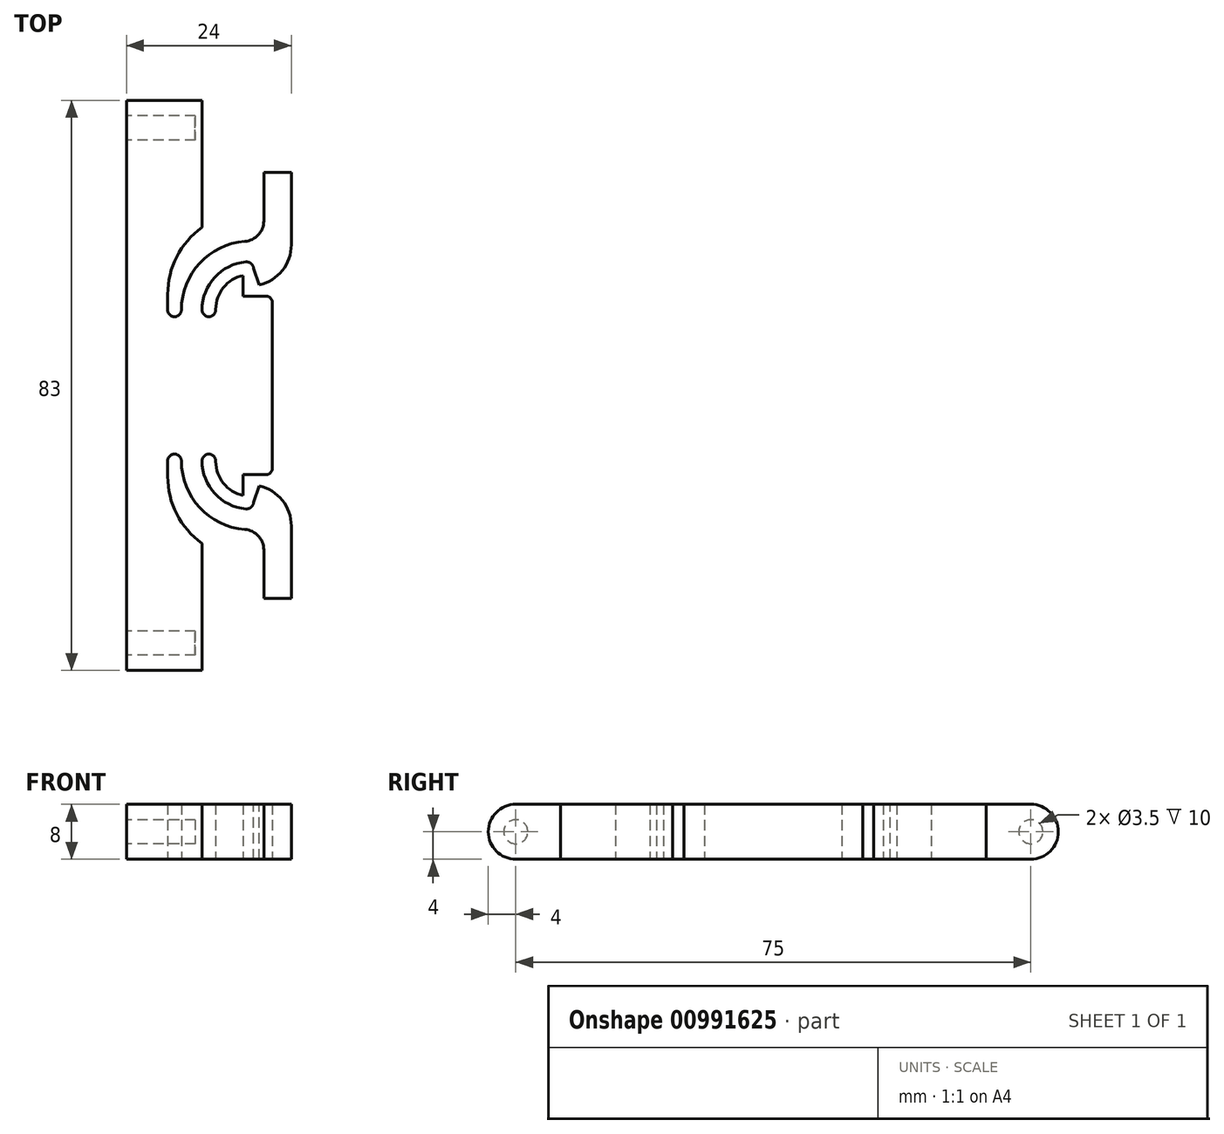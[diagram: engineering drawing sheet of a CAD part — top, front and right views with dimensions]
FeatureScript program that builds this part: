
annotation { "Feature Type Name" : "Feature", "Feature Type Description" : "" }
export const myFeature = defineFeature(function(context is Context, id is Id, definition is map)
    precondition{}
    {
        {
            var Q0;
            Q0=qCreatedBy(makeId("Top.planeOp"),FACE);
            var sketch = newSketch(context, id + "F0", { "sketchPlane" : qUnion([Q0])});
            skLineSegment(sketch, "E0.bottom", {"start": v(0, 0) * mm, "end": v(24, 0) * mm});
            skLineSegment(sketch, "E0.top", {"start": v(0, 83) * mm, "end": v(24, 83) * mm});
            skLineSegment(sketch, "E0.left", {"start": v(0, 0) * mm, "end": v(0, 83) * mm});
            skLineSegment(sketch, "E0.right", {"start": v(24, 0) * mm, "end": v(24, 83) * mm});
            skLineSegment(sketch, "E1", {"start": v(0, 41.5) * mm, "end": v(24, 41.5) * mm, "construction": true});
            skLineSegment(sketch, "E2.bottom", {"start": v(24, 59.5) * mm, "end": v(17, 59.5) * mm});
            skLineSegment(sketch, "E2.top", {"start": v(24, 23.5) * mm, "end": v(17, 23.5) * mm});
            skLineSegment(sketch, "E2.left", {"start": v(24, 59.5) * mm, "end": v(24, 23.5) * mm});
            skLineSegment(sketch, "E2.right", {"start": v(17, 59.5) * mm, "end": v(17, 23.5) * mm});
            skLineSegment(sketch, "E3", {"start": v(18.5, 59.5) * mm, "end": v(18.5, 23.5) * mm, "construction": true});
            skLineSegment(sketch, "E4.bottom", {"start": v(18.5, 59.5) * mm, "end": v(24, 59.5) * mm});
            skLineSegment(sketch, "E4.top", {"start": v(18.5, 56) * mm, "end": v(24, 56) * mm});
            skLineSegment(sketch, "E4.left", {"start": v(18.5, 59.5) * mm, "end": v(18.5, 56) * mm});
            skLineSegment(sketch, "E4.right", {"start": v(24, 59.5) * mm, "end": v(24, 56) * mm});
            skLineSegment(sketch, "E5.bottom", {"start": v(18.5, 23.5) * mm, "end": v(24, 23.5) * mm});
            skLineSegment(sketch, "E5.top", {"start": v(18.5, 27) * mm, "end": v(24, 27) * mm});
            skLineSegment(sketch, "E5.left", {"start": v(18.5, 23.5) * mm, "end": v(18.5, 27) * mm});
            skLineSegment(sketch, "E5.right", {"start": v(24, 23.5) * mm, "end": v(24, 27) * mm});
            skLineSegment(sketch, "E6", {"start": v(11, 83) * mm, "end": v(11, 0) * mm, "construction": true});
            skLineSegment(sketch, "E7.bottom", {"start": v(11, 64.5) * mm, "end": v(24, 64.5) * mm});
            skLineSegment(sketch, "E7.top", {"start": v(11, 62.5) * mm, "end": v(24, 62.5) * mm});
            skLineSegment(sketch, "E7.left", {"start": v(11, 64.5) * mm, "end": v(11, 62.5) * mm});
            skLineSegment(sketch, "E7.right", {"start": v(24, 64.5) * mm, "end": v(24, 62.5) * mm});
            skLineSegment(sketch, "E8.bottom", {"start": v(11, 20.5) * mm, "end": v(24, 20.5) * mm});
            skLineSegment(sketch, "E8.top", {"start": v(11, 18.5) * mm, "end": v(24, 18.5) * mm});
            skLineSegment(sketch, "E8.left", {"start": v(11, 20.5) * mm, "end": v(11, 18.5) * mm});
            skLineSegment(sketch, "E8.right", {"start": v(24, 20.5) * mm, "end": v(24, 18.5) * mm});
            skLineSegment(sketch, "E9.bottom", {"start": v(20, 62.5) * mm, "end": v(24, 62.5) * mm});
            skLineSegment(sketch, "E9.top", {"start": v(20, 72.5) * mm, "end": v(24, 72.5) * mm});
            skLineSegment(sketch, "E9.left", {"start": v(20, 62.5) * mm, "end": v(20, 72.5) * mm});
            skLineSegment(sketch, "E9.right", {"start": v(24, 62.5) * mm, "end": v(24, 72.5) * mm});
            skLineSegment(sketch, "E10.bottom", {"start": v(20, 20.5) * mm, "end": v(24, 20.5) * mm});
            skLineSegment(sketch, "E10.top", {"start": v(20, 10.5) * mm, "end": v(24, 10.5) * mm});
            skLineSegment(sketch, "E10.left", {"start": v(20, 20.5) * mm, "end": v(20, 10.5) * mm});
            skLineSegment(sketch, "E10.right", {"start": v(24, 20.5) * mm, "end": v(24, 10.5) * mm});
            skLineSegment(sketch, "E11.top", {"start": v(11, 73) * mm, "end": v(24, 73) * mm});
            skLineSegment(sketch, "E11.left", {"start": v(11, 64.5) * mm, "end": v(11, 73) * mm});
            skLineSegment(sketch, "E11.right", {"start": v(24, 64.5) * mm, "end": v(24, 73) * mm});
            skLineSegment(sketch, "E12.top", {"start": v(11, 10) * mm, "end": v(24, 10) * mm});
            skLineSegment(sketch, "E12.left", {"start": v(11, 18.5) * mm, "end": v(11, 10) * mm});
            skLineSegment(sketch, "E12.right", {"start": v(24, 18.5) * mm, "end": v(24, 10) * mm});
            skLineSegment(sketch, "E13.bottom", {"start": v(17, 59.5) * mm, "end": v(11, 59.5) * mm});
            skLineSegment(sketch, "E13.top", {"start": v(17, 57.5) * mm, "end": v(11, 57.5) * mm});
            skLineSegment(sketch, "E13.left", {"start": v(17, 59.5) * mm, "end": v(17, 57.5) * mm});
            skLineSegment(sketch, "E13.right", {"start": v(11, 59.5) * mm, "end": v(11, 57.5) * mm});
            skLineSegment(sketch, "E14.bottom", {"start": v(17, 23.5) * mm, "end": v(11, 23.5) * mm});
            skLineSegment(sketch, "E14.top", {"start": v(17, 25.5) * mm, "end": v(11, 25.5) * mm});
            skLineSegment(sketch, "E14.left", {"start": v(17, 23.5) * mm, "end": v(17, 25.5) * mm});
            skLineSegment(sketch, "E14.right", {"start": v(11, 23.5) * mm, "end": v(11, 25.5) * mm});
            skLineSegment(sketch, "E15.bottom", {"start": v(11, 57.5) * mm, "end": v(13, 57.5) * mm});
            skLineSegment(sketch, "E15.top", {"start": v(11, 51.5) * mm, "end": v(13, 51.5) * mm});
            skLineSegment(sketch, "E15.left", {"start": v(11, 57.5) * mm, "end": v(11, 51.5) * mm});
            skLineSegment(sketch, "E15.right", {"start": v(13, 57.5) * mm, "end": v(13, 51.5) * mm});
            skLineSegment(sketch, "E16.bottom", {"start": v(11, 25.5) * mm, "end": v(13, 25.5) * mm});
            skLineSegment(sketch, "E16.top", {"start": v(11, 31.5) * mm, "end": v(13, 31.5) * mm});
            skLineSegment(sketch, "E16.left", {"start": v(11, 25.5) * mm, "end": v(11, 31.5) * mm});
            skLineSegment(sketch, "E16.right", {"start": v(13, 25.5) * mm, "end": v(13, 31.5) * mm});
            skLineSegment(sketch, "E17.bottom", {"start": v(8, 20.5) * mm, "end": v(11, 20.5) * mm});
            skLineSegment(sketch, "E17.top", {"start": v(8, 31.5) * mm, "end": v(11, 31.5) * mm});
            skLineSegment(sketch, "E17.left", {"start": v(8, 20.5) * mm, "end": v(8, 31.5) * mm});
            skLineSegment(sketch, "E17.right", {"start": v(11, 20.5) * mm, "end": v(11, 31.5) * mm});
            skPoint(sketch, "E18.oppositeSnap0", {"position": v(8, 26) * mm});
            skLineSegment(sketch, "E18.bottom", {"start": v(11, 51.5) * mm, "end": v(8, 51.5) * mm});
            skLineSegment(sketch, "E18.top", {"start": v(11, 62.5) * mm, "end": v(8, 62.5) * mm});
            skLineSegment(sketch, "E18.left", {"start": v(11, 51.5) * mm, "end": v(11, 62.5) * mm});
            skLineSegment(sketch, "E18.right", {"start": v(8, 51.5) * mm, "end": v(8, 62.5) * mm});
            skLineSegment(sketch, "E19.bottom", {"start": v(11, 18.5) * mm, "end": v(6, 18.5) * mm});
            skLineSegment(sketch, "E19.top", {"start": v(11, 31.5) * mm, "end": v(6, 31.5) * mm});
            skLineSegment(sketch, "E19.left", {"start": v(11, 18.5) * mm, "end": v(11, 31.5) * mm});
            skLineSegment(sketch, "E19.right", {"start": v(6, 18.5) * mm, "end": v(6, 31.5) * mm});
            skLineSegment(sketch, "E20.bottom", {"start": v(11, 64.5) * mm, "end": v(6, 64.5) * mm});
            skLineSegment(sketch, "E20.top", {"start": v(11, 51.5) * mm, "end": v(6, 51.5) * mm});
            skLineSegment(sketch, "E20.left", {"start": v(11, 64.5) * mm, "end": v(11, 51.5) * mm});
            skLineSegment(sketch, "E20.right", {"start": v(6, 64.5) * mm, "end": v(6, 51.5) * mm});
            skLineSegment(sketch, "E21.top", {"start": v(11, 0) * mm, "end": v(24, 0) * mm});
            skLineSegment(sketch, "E21.left", {"start": v(11, 10) * mm, "end": v(11, 0) * mm});
            skLineSegment(sketch, "E21.right", {"start": v(24, 10) * mm, "end": v(24, 0) * mm});
            skLineSegment(sketch, "E22.top", {"start": v(11, 83) * mm, "end": v(24, 83) * mm});
            skLineSegment(sketch, "E22.left", {"start": v(11, 73) * mm, "end": v(11, 83) * mm});
            skLineSegment(sketch, "E22.right", {"start": v(24, 73) * mm, "end": v(24, 83) * mm});
            skPoint(sketch, "E23.oppositeSnap0", {"position": v(21.25, 27) * mm});
            skLineSegment(sketch, "E23.bottom", {"start": v(17, 54.5) * mm, "end": v(21.25, 54.5) * mm});
            skLineSegment(sketch, "E23.top", {"start": v(17, 28.5) * mm, "end": v(21.25, 28.5) * mm});
            skLineSegment(sketch, "E23.left", {"start": v(17, 54.5) * mm, "end": v(17, 28.5) * mm});
            skLineSegment(sketch, "E23.right", {"start": v(21.25, 54.5) * mm, "end": v(21.25, 28.5) * mm});
            skSolve(sketch);
        }
        {
            var Q0;
            {var subQ7=sQuery(id+"F0.wireOp",EDGE,"E0.left");Q0=makeQuery(id+"F0.imprint","IMPRINT",FACE,{"disambiguationData":[TD([[makeQuery(id+"F0.imprint","IMPRINT",EDGE,{"derivedFrom":subQ7}),-1.0]])]});}
            var Q1;
            {var subQ3=sQuery(id+"F0.wireOp",EDGE,"E9.top");Q1=makeQuery(id+"F0.imprint","IMPRINT",FACE,{"disambiguationData":[TD([[makeQuery(id+"F0.imprint","IMPRINT",EDGE,{"derivedFrom":subQ3}),-1.0]])]});}
            var Q2;
            {var subQ0=sQuery(id+"F0.wireOp",EDGE,"E7.bottom");var subQ1=sQuery(id+"F0.wireOp",EDGE,"E0.right");var subQ2=makeQuery(id+"F0.imprint","INTERSECT",VERTEX,{"derivedFrom":[subQ1,subQ0]});Q2=makeQuery(id+"F0.imprint","IMPRINT",FACE,{"disambiguationData":[TD([[makeQuery(id+"F0.imprint","IMPRINT",EDGE,{"disambiguationData":[TD([[subQ2,1.0]])],"derivedFrom":subQ1}),1.0]])]});}
            var Q3;
            {var subQ3=sQuery(id+"F0.wireOp",EDGE,"E4.top");Q3=makeQuery(id+"F0.imprint","IMPRINT",FACE,{"disambiguationData":[TD([[makeQuery(id+"F0.imprint","IMPRINT",EDGE,{"derivedFrom":subQ3}),1.0]])]});}
            var Q4;
            {var subQ0=sQuery(id+"F0.wireOp",EDGE,"E5.top");Q4=makeQuery(id+"F0.imprint","IMPRINT",FACE,{"disambiguationData":[TD([[makeQuery(id+"F0.imprint","IMPRINT",EDGE,{"derivedFrom":subQ0}),-1.0]])]});}
            var Q5;
            {var subQ0=sQuery(id+"F0.wireOp",EDGE,"E8.bottom");var subQ1=sQuery(id+"F0.wireOp",EDGE,"E0.right");var subQ2=makeQuery(id+"F0.imprint","INTERSECT",VERTEX,{"derivedFrom":[subQ1,subQ0]});Q5=makeQuery(id+"F0.imprint","IMPRINT",FACE,{"disambiguationData":[TD([[makeQuery(id+"F0.imprint","IMPRINT",EDGE,{"disambiguationData":[TD([[subQ2,1.0]])],"derivedFrom":subQ1}),1.0]])]});}
            var Q6;
            {var subQ0=sQuery(id+"F0.wireOp",EDGE,"E10.top");Q6=makeQuery(id+"F0.imprint","IMPRINT",FACE,{"disambiguationData":[TD([[makeQuery(id+"F0.imprint","IMPRINT",EDGE,{"derivedFrom":subQ0}),1.0]])]});}
            var Q7;
            {var subQ3=sQuery(id+"F0.wireOp",EDGE,"E14.bottom");Q7=makeQuery(id+"F0.imprint","IMPRINT",FACE,{"disambiguationData":[TD([[makeQuery(id+"F0.imprint","IMPRINT",EDGE,{"derivedFrom":subQ3}),1.0]])]});}
            var Q8;
            Q8=makeQuery(id+"F0.imprint","IMPRINT",FACE,{"disambiguationData":[TD([[makeQuery(id+"F0.imprint","IMPRINT",EDGE,{"derivedFrom":sQuery(id+"F0.wireOp",EDGE,"E14.right")}),1.0]])]});
            var Q9;
            Q9=makeQuery(id+"F0.imprint","IMPRINT",FACE,{"disambiguationData":[TD([[makeQuery(id+"F0.imprint","IMPRINT",EDGE,{"derivedFrom":sQuery(id+"F0.wireOp",EDGE,"E13.right")}),-1.0]])]});
            var Q10;
            {var subQ0=sQuery(id+"F0.wireOp",EDGE,"E13.bottom");Q10=makeQuery(id+"F0.imprint","IMPRINT",FACE,{"disambiguationData":[TD([[makeQuery(id+"F0.imprint","IMPRINT",EDGE,{"derivedFrom":subQ0}),-1.0]])]});}
            var Q11;
            {var subQ0=sQuery(id+"F0.wireOp",EDGE,"E23.bottom");Q11=makeQuery(id+"F0.imprint","IMPRINT",FACE,{"disambiguationData":[TD([[makeQuery(id+"F0.imprint","IMPRINT",EDGE,{"derivedFrom":subQ0}),-1.0]])]});}
            extrude(context, id + "F1", {"entities" : qUnion([Q0, Q1, Q2, Q3, Q4, Q5, Q6, Q7, Q8, Q9, Q10, Q11]), "depth" : 8 * mm, "offsetDistance" : 25 * mm});
        }
        {
            var Q0;
            Q0=makeQuery(id+"F1.opExtrude","CAP_EDGE",EDGE,{"disambiguationData":[OSD([sQuery(id+"F0.wireOp",EDGE,"E0.top")])],"isStart":false});
            var Q1;
            Q1=makeQuery(id+"F1.opExtrude","CAP_EDGE",EDGE,{"disambiguationData":[OSD([sQuery(id+"F0.wireOp",EDGE,"E0.bottom")])],"isStart":false});
            var Q2;
            Q2=makeQuery(id+"F1.opExtrude","CAP_EDGE",EDGE,{"disambiguationData":[OSD([sQuery(id+"F0.wireOp",EDGE,"E0.bottom")])],"isStart":true});
            var Q3;
            Q3=makeQuery(id+"F1.opExtrude","CAP_EDGE",EDGE,{"disambiguationData":[OSD([sQuery(id+"F0.wireOp",EDGE,"E0.top")])],"isStart":true});
            fillet(context, id + "F2", {"entities" : qUnion([Q0, Q1, Q2, Q3]), "radius" : 4 * mm, "tangentPropagation" : true, "allowEdgeOverflow" : false});
        }
        {
            var Q0;
            Q0=makeQuery(id+"F1.opExtrude","SWEPT_EDGE",EDGE,{"disambiguationData":[OSD([sQuery(id+"F0.wireOp",EDGE,"E0.right"),sQuery(id+"F0.wireOp",EDGE,"E4.top")])]});
            var Q1;
            Q1=makeQuery(id+"F1.opExtrude","SWEPT_EDGE",EDGE,{"disambiguationData":[OSD([sQuery(id+"F0.wireOp",EDGE,"E0.right"),sQuery(id+"F0.wireOp",EDGE,"E5.top")])]});
            fillet(context, id + "F3", {"entities" : qUnion([Q0, Q1]), "radius" : 6 * mm, "tangentPropagation" : true, "allowEdgeOverflow" : false});
        }
        {
            var Q0;
            Q0=makeQuery(id+"F3.opFillet","BLEND_EDGE",EDGE,{"blendedFrom":[makeQuery(id+"F1.opExtrude","SWEPT_EDGE",EDGE,{"disambiguationData":[OSD([sQuery(id+"F0.wireOp",EDGE,"E0.right"),sQuery(id+"F0.wireOp",EDGE,"E4.top")])]}),makeQuery(id+"F1.opExtrude","SWEPT_FACE",FACE,{"disambiguationData":[OSD([sQuery(id+"F0.wireOp",EDGE,"E4.left")])]})],"blendedInto":[makeQuery(id+"F1.opExtrude","SWEPT_FACE",FACE,{"disambiguationData":[OSD([sQuery(id+"F0.wireOp",EDGE,"E4.left")])]})]});
            chamfer(context, id + "F4", {"entities" : qUnion([Q0]), "chamferType" : ChamferType.TWO_OFFSETS, "width1" : 0.5 * mm, "oppositeDirection" : false, "width2" : 2.5 * mm, "tangentPropagation" : true});
        }
        {
            var Q0;
            Q0=makeQuery(id+"F3.opFillet","BLEND_EDGE",EDGE,{"blendedFrom":[makeQuery(id+"F1.opExtrude","SWEPT_EDGE",EDGE,{"disambiguationData":[OSD([sQuery(id+"F0.wireOp",EDGE,"E0.right"),sQuery(id+"F0.wireOp",EDGE,"E5.top")])]}),makeQuery(id+"F1.opExtrude","SWEPT_FACE",FACE,{"disambiguationData":[OSD([sQuery(id+"F0.wireOp",EDGE,"E5.left")])]})],"blendedInto":[makeQuery(id+"F1.opExtrude","SWEPT_FACE",FACE,{"disambiguationData":[OSD([sQuery(id+"F0.wireOp",EDGE,"E5.left")])]})]});
            chamfer(context, id + "F5", {"entities" : qUnion([Q0]), "chamferType" : ChamferType.TWO_OFFSETS, "width1" : 0.5 * mm, "oppositeDirection" : true, "width2" : 2.5 * mm, "tangentPropagation" : true});
        }
        {
            var Q0;
            Q0=makeQuery(id+"F1.opExtrude","SWEPT_FACE",FACE,{"disambiguationData":[OSD([sQuery(id+"F0.wireOp",EDGE,"E0.left")])]});
            var sketch = newSketch(context, id + "F6", { "sketchPlane" : qUnion([Q0])});
            skLineSegment(sketch, "E24", {"start": v(-83, 4) * mm, "end": v(0, 4) * mm, "construction": true});
            skCircle(sketch, "E25", {"center": v(-79, 4) * mm, "radius": 1.75 * mm});
            skCircle(sketch, "E26", {"center": v(-4, 4) * mm, "radius": 1.75 * mm});
            skSolve(sketch);
        }
        {
            var Q0;
            Q0=qSketchRegion(id+"F6",true);
            extrude(context, id + "F7", {"entities" : qUnion([Q0]), "operationType" : NewBodyOperationType.REMOVE, "oppositeDirection" : true, "depth" : 10 * mm, "offsetDistance" : 25 * mm});
        }
        {
            var Q0;
            Q0=makeQuery(id+"F1.opExtrude","SWEPT_EDGE",EDGE,{"disambiguationData":[OSD([sQuery(id+"F0.wireOp",EDGE,"E13.top"),sQuery(id+"F0.wireOp",EDGE,"E15.right")])]});
            var Q1;
            Q1=makeQuery(id+"F1.opExtrude","SWEPT_EDGE",EDGE,{"disambiguationData":[OSD([sQuery(id+"F0.wireOp",EDGE,"E14.top"),sQuery(id+"F0.wireOp",EDGE,"E16.right")])]});
            fillet(context, id + "F8", {"entities" : qUnion([Q0, Q1]), "radius" : 5 * mm, "tangentPropagation" : true, "allowEdgeOverflow" : false});
        }
        {
            var Q0;
            Q0=makeQuery(id+"F1.opExtrude","SWEPT_EDGE",EDGE,{"disambiguationData":[OSD([sQuery(id+"F0.wireOp",EDGE,"E13.bottom"),sQuery(id+"F0.wireOp",EDGE,"E13.right"),sQuery(id+"F0.wireOp",EDGE,"E18.left")])]});
            var Q1;
            Q1=makeQuery(id+"F1.opExtrude","SWEPT_EDGE",EDGE,{"disambiguationData":[OSD([sQuery(id+"F0.wireOp",EDGE,"E14.bottom"),sQuery(id+"F0.wireOp",EDGE,"E14.right"),sQuery(id+"F0.wireOp",EDGE,"E17.right")])]});
            fillet(context, id + "F9", {"entities" : qUnion([Q0, Q1]), "radius" : 7 * mm, "tangentPropagation" : true, "allowEdgeOverflow" : false});
        }
        {
            var Q0;
            Q0=makeQuery(id+"F1.opExtrude","SWEPT_EDGE",EDGE,{"disambiguationData":[OSD([sQuery(id+"F0.wireOp",EDGE,"E18.top"),sQuery(id+"F0.wireOp",EDGE,"E18.right")])]});
            var Q1;
            Q1=makeQuery(id+"F1.opExtrude","SWEPT_EDGE",EDGE,{"disambiguationData":[OSD([sQuery(id+"F0.wireOp",EDGE,"E17.bottom"),sQuery(id+"F0.wireOp",EDGE,"E17.left")])]});
            fillet(context, id + "F10", {"entities" : qUnion([Q0, Q1]), "radius" : 10 * mm, "tangentPropagation" : true, "allowEdgeOverflow" : false});
        }
        {
            var Q0;
            Q0=makeQuery(id+"F1.opExtrude","SWEPT_EDGE",EDGE,{"disambiguationData":[OSD([sQuery(id+"F0.wireOp",EDGE,"E20.bottom"),sQuery(id+"F0.wireOp",EDGE,"E20.right")])]});
            var Q1;
            Q1=makeQuery(id+"F1.opExtrude","SWEPT_EDGE",EDGE,{"disambiguationData":[OSD([sQuery(id+"F0.wireOp",EDGE,"E19.bottom"),sQuery(id+"F0.wireOp",EDGE,"E19.right")])]});
            fillet(context, id + "F11", {"entities" : qUnion([Q0, Q1]), "radius" : 12 * mm, "tangentPropagation" : true, "allowEdgeOverflow" : false});
        }
        {
            var Q0;
            Q0=makeQuery(id+"F1.opExtrude","SWEPT_EDGE",EDGE,{"disambiguationData":[OSD([sQuery(id+"F0.wireOp",EDGE,"E7.top"),sQuery(id+"F0.wireOp",EDGE,"E9.left")])]});
            var Q1;
            Q1=makeQuery(id+"F1.opExtrude","SWEPT_EDGE",EDGE,{"disambiguationData":[OSD([sQuery(id+"F0.wireOp",EDGE,"E8.bottom"),sQuery(id+"F0.wireOp",EDGE,"E10.left")])]});
            fillet(context, id + "F12", {"entities" : qUnion([Q0, Q1]), "radius" : 3 * mm, "tangentPropagation" : true, "allowEdgeOverflow" : false});
        }
        {
            var Q0;
            Q0=makeQuery(id+"F1.opExtrude","SWEPT_EDGE",EDGE,{"disambiguationData":[OSD([sQuery(id+"F0.wireOp",EDGE,"E15.top"),sQuery(id+"F0.wireOp",EDGE,"E15.right")])]});
            var Q1;
            Q1=makeQuery(id+"F1.opExtrude","SWEPT_EDGE",EDGE,{"disambiguationData":[OSD([sQuery(id+"F0.wireOp",EDGE,"E15.top"),sQuery(id+"F0.wireOp",EDGE,"E15.left"),sQuery(id+"F0.wireOp",EDGE,"E18.bottom")])]});
            var Q2;
            Q2=makeQuery(id+"F1.opExtrude","SWEPT_EDGE",EDGE,{"disambiguationData":[OSD([sQuery(id+"F0.wireOp",EDGE,"E18.bottom"),sQuery(id+"F0.wireOp",EDGE,"E18.right"),sQuery(id+"F0.wireOp",EDGE,"E20.top")])]});
            var Q3;
            Q3=makeQuery(id+"F1.opExtrude","SWEPT_EDGE",EDGE,{"disambiguationData":[OSD([sQuery(id+"F0.wireOp",EDGE,"E20.top"),sQuery(id+"F0.wireOp",EDGE,"E20.right")])]});
            var Q4;
            Q4=makeQuery(id+"F1.opExtrude","SWEPT_EDGE",EDGE,{"disambiguationData":[OSD([sQuery(id+"F0.wireOp",EDGE,"E16.top"),sQuery(id+"F0.wireOp",EDGE,"E16.right")])]});
            var Q5;
            Q5=makeQuery(id+"F1.opExtrude","SWEPT_EDGE",EDGE,{"disambiguationData":[OSD([sQuery(id+"F0.wireOp",EDGE,"E16.top"),sQuery(id+"F0.wireOp",EDGE,"E16.left"),sQuery(id+"F0.wireOp",EDGE,"E17.top")])]});
            var Q6;
            Q6=makeQuery(id+"F1.opExtrude","SWEPT_EDGE",EDGE,{"disambiguationData":[OSD([sQuery(id+"F0.wireOp",EDGE,"E19.top"),sQuery(id+"F0.wireOp",EDGE,"E19.right")])]});
            var Q7;
            Q7=makeQuery(id+"F10.opFillet","BLEND_EDGE",EDGE,{"blendedFrom":[makeQuery(id+"F1.opExtrude","SWEPT_EDGE",EDGE,{"disambiguationData":[OSD([sQuery(id+"F0.wireOp",EDGE,"E17.bottom"),sQuery(id+"F0.wireOp",EDGE,"E17.left")])]}),makeQuery(id+"F1.opExtrude","SWEPT_FACE",FACE,{"disambiguationData":[OSD([sQuery(id+"F0.wireOp",EDGE,"E19.top")])]})],"blendedInto":[makeQuery(id+"F1.opExtrude","SWEPT_FACE",FACE,{"disambiguationData":[OSD([sQuery(id+"F0.wireOp",EDGE,"E19.top")])]})]});
            var Q8;
            Q8=makeQuery(id+"F1.opExtrude","SWEPT_EDGE",EDGE,{"disambiguationData":[OSD([sQuery(id+"F0.wireOp",EDGE,"E2.top"),sQuery(id+"F0.wireOp",EDGE,"E5.left")])]});
            var Q9;
            Q9=makeQuery(id+"F1.opExtrude","SWEPT_EDGE",EDGE,{"disambiguationData":[OSD([sQuery(id+"F0.wireOp",EDGE,"E2.bottom"),sQuery(id+"F0.wireOp",EDGE,"E4.left")])]});
            var Q10;
            Q10=makeQuery(id+"F1.opExtrude","SWEPT_EDGE",EDGE,{"disambiguationData":[OSD([sQuery(id+"F0.wireOp",EDGE,"E17.top"),sQuery(id+"F0.wireOp",EDGE,"E17.left"),sQuery(id+"F0.wireOp",EDGE,"E19.top")])]});
            fillet(context, id + "F13", {"entities" : qUnion([Q0, Q1, Q2, Q3, Q4, Q5, Q6, Q7, Q8, Q9, Q10]), "radius" : 1 * mm, "tangentPropagation" : true, "allowEdgeOverflow" : false});
        }
        {
            var Q0;
            Q0=makeQuery(id+"F1.opExtrude","SWEPT_EDGE",EDGE,{"disambiguationData":[OSD([sQuery(id+"F0.wireOp",EDGE,"E23.top"),sQuery(id+"F0.wireOp",EDGE,"E23.right")])]});
            var Q1;
            Q1=makeQuery(id+"F1.opExtrude","SWEPT_EDGE",EDGE,{"disambiguationData":[OSD([sQuery(id+"F0.wireOp",EDGE,"E23.bottom"),sQuery(id+"F0.wireOp",EDGE,"E23.right")])]});
            fillet(context, id + "F14", {"entities" : qUnion([Q0, Q1]), "radius" : 1 * mm, "tangentPropagation" : true, "allowEdgeOverflow" : false});
        }
    });
